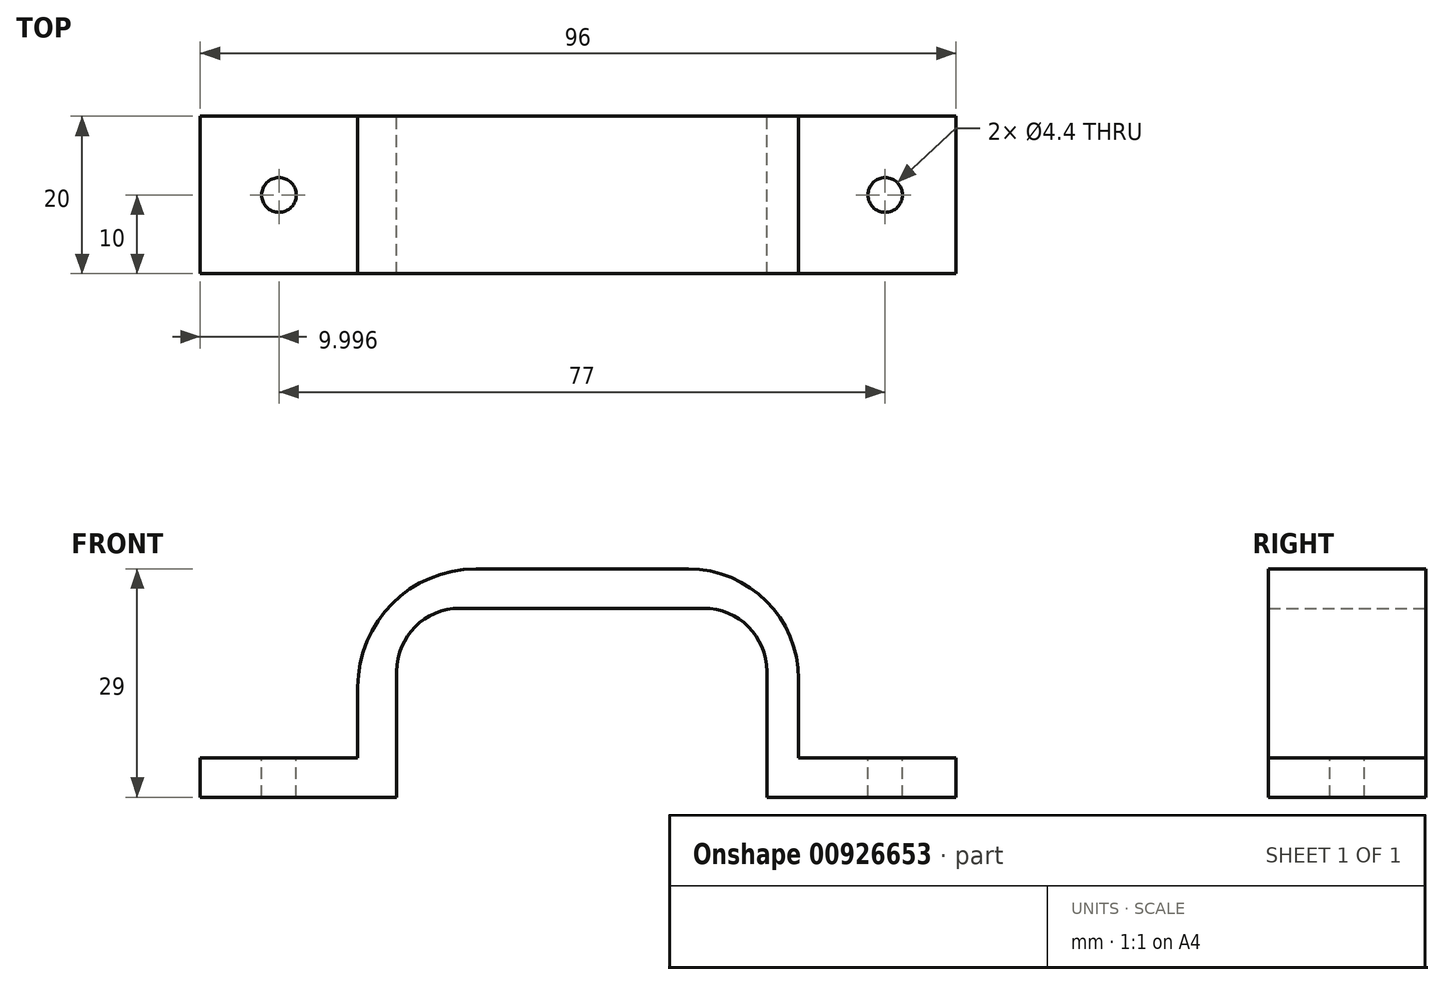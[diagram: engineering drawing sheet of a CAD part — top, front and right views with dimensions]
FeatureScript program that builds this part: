
annotation { "Feature Type Name" : "Feature", "Feature Type Description" : "" }
export const myFeature = defineFeature(function(context is Context, id is Id, definition is map)
    precondition{}
    {
        {
            var Q0;
            Q0=qCreatedBy(makeId("Front.planeOp"),FACE);
            var sketch = newSketch(context, id + "F0", { "sketchPlane" : qUnion([Q0])});
            skLineSegment(sketch, "E0.bottom", {"start": v(-15.5, 12) * mm, "end": v(15.5, 12) * mm});
            skLineSegment(sketch, "E0.left", {"start": v(-23.5, 4) * mm, "end": v(-23.5, -12) * mm});
            skLineSegment(sketch, "E0.right", {"start": v(23.5, 4) * mm, "end": v(23.5, -12) * mm});
            skPoint(sketch, "E0.middle", {"position": v(0, 0) * mm});
            skPoint(sketch, "E1.visualSharp", {"position": v(-23.5, 12) * mm});
            skArc(sketch, "E1.filletArc", {"start": v(-15.5, 12) * mm, "mid": v(-21.16, 9.66) * mm, "end": v(-23.5, 4) * mm});
            skPoint(sketch, "E2.visualSharp", {"position": v(23.5, 12) * mm});
            skArc(sketch, "E2.filletArc", {"start": v(23.5, 4) * mm, "mid": v(21.16, 9.66) * mm, "end": v(15.5, 12) * mm});
            skLineSegment(sketch, "E3.top", {"start": v(-13.45, 17) * mm, "end": v(13.55, 17) * mm});
            skPoint(sketch, "E4.visualSharp", {"position": v(-28.45, 17) * mm});
            skArc(sketch, "E4.filletArc", {"start": v(-13.45, 17) * mm, "mid": v(-24.06, 12.6) * mm, "end": v(-28.45, 2) * mm});
            skPoint(sketch, "E5.visualSharp", {"position": v(28.55, 17) * mm});
            skArc(sketch, "E5.filletArc", {"start": v(27.55, 3) * mm, "mid": v(23.45, 12.9) * mm, "end": v(13.55, 17) * mm});
            skLineSegment(sketch, "E6", {"start": v(-23.5, -12) * mm, "end": v(-28.45, -12) * mm});
            skLineSegment(sketch, "E7", {"start": v(23.5, -12) * mm, "end": v(27.55, -12) * mm});
            skLineSegment(sketch, "E8", {"start": v(-28.45, 2) * mm, "end": v(-28.45, -12) * mm});
            skLineSegment(sketch, "E9", {"start": v(27.55, 3) * mm, "end": v(27.55, -12) * mm});
            skLineSegment(sketch, "E10", {"start": v(-48.45, -12) * mm, "end": v(-28.45, -12) * mm});
            skLineSegment(sketch, "E11", {"start": v(27.55, -12) * mm, "end": v(47.55, -12) * mm});
            skLineSegment(sketch, "E12", {"start": v(47.55, -12) * mm, "end": v(47.55, -7) * mm});
            skLineSegment(sketch, "E13", {"start": v(47.55, -7) * mm, "end": v(27.55, -7) * mm});
            skLineSegment(sketch, "E14", {"start": v(-48.45, -12) * mm, "end": v(-48.45, -7) * mm});
            skLineSegment(sketch, "E15", {"start": v(-48.45, -7) * mm, "end": v(-28.45, -7) * mm});
            skSolve(sketch);
        }
        {
            var Q0;
            Q0 = qSketchRegion(id + "F0", true);
            extrude(context, id + "F1", {"entities" : qUnion([Q0]), "depth" : 20 * mm, "offsetDistance" : 25 * mm});
        }
        {
            var Q0;
            Q0=makeQuery(id+"F1.opExtrude","SWEPT_FACE",FACE,{"disambiguationData":[OSD([sQuery(id+"F0.wireOp",EDGE,"E15")])]});
            var sketch = newSketch(context, id + "F2", { "sketchPlane" : qUnion([Q0])});
            skPoint(sketch, "E16", {"position": v(-38.45, -10) * mm});
            skCircle(sketch, "E17", {"center": v(-38.45, -10) * mm, "radius": 2.2 * mm});
            skPoint(sketch, "E18", {"position": v(38.55, -10) * mm});
            skCircle(sketch, "E19", {"center": v(38.55, -10) * mm, "radius": 2.2 * mm});
            skSolve(sketch);
        }
        {
            var Q0;
            Q0=makeQuery(id+"F2.imprint","IMPRINT",FACE,{"disambiguationData":[TD([[makeQuery(id+"F2.imprint","IMPRINT",EDGE,{"derivedFrom":sQuery(id+"F2.wireOp",EDGE,"E19")}),1.0]])]});
            var Q1;
            Q1=makeQuery(id+"F2.imprint","IMPRINT",FACE,{"disambiguationData":[TD([[makeQuery(id+"F2.imprint","IMPRINT",EDGE,{"derivedFrom":sQuery(id+"F2.wireOp",EDGE,"E17")}),1.0]])]});
            extrude(context, id + "F3", {"entities" : qUnion([Q0, Q1]), "operationType" : NewBodyOperationType.REMOVE, "oppositeDirection" : true, "depth" : 50 * mm, "offsetDistance" : 25 * mm});
        }
    });
